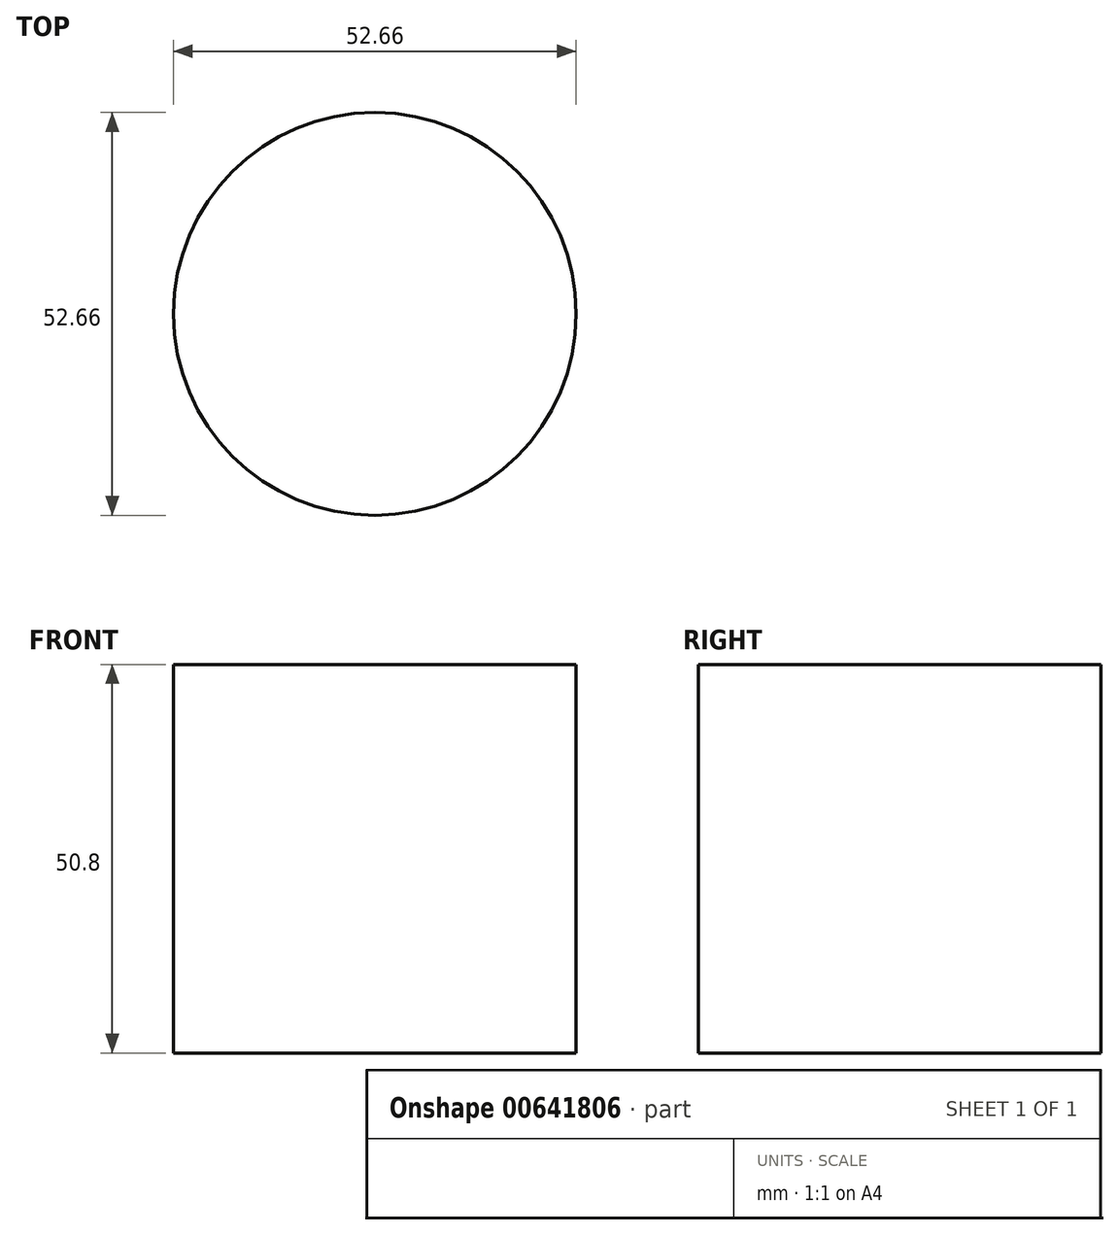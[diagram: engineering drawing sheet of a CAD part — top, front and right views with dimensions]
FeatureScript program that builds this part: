
annotation { "Feature Type Name" : "Feature", "Feature Type Description" : "" }
export const myFeature = defineFeature(function(context is Context, id is Id, definition is map)
    precondition{}
    {
        {
            var Q0;
            Q0=qCreatedBy(makeId("Top.planeOp"),FACE);
            var sketch = newSketch(context, id + "F0", { "sketchPlane" : qUnion([Q0])});
            skCircle(sketch, "E0", {"center": v(-45.91, 43.3) * mm, "radius": 26.33 * mm});
            skLineSegment(sketch, "E1", {"start": v(-63.2, 63.17) * mm, "end": v(-28.63, 23.45) * mm});
            skLineSegment(sketch, "E2", {"start": v(-38.25, 34.5) * mm, "end": v(-56.05, 19.01) * mm});
            skLineSegment(sketch, "E3", {"start": v(-54.32, 52.97) * mm, "end": v(-71.67, 37.87) * mm});
            skLineSegment(sketch, "E4", {"start": v(-28.63, 23.45) * mm, "end": v(-38.25, 34.5) * mm});
            skLineSegment(sketch, "E5", {"start": v(-63.2, 63.17) * mm, "end": v(-52.87, 51.3) * mm});
            skLineSegment(sketch, "E6", {"start": v(-52.87, 51.3) * mm, "end": v(-63.2, 63.17) * mm});
            skSolve(sketch);
        }
        {
            var Q0;
            {var subQ1=sQuery(id+"F0.wireOp",EDGE,"E1");Q0=makeQuery(id+"F0.imprint","IMPRINT",FACE,{"disambiguationData":[TD([[makeQuery(id+"F0.imprint","IMPRINT",EDGE,{"derivedFrom":subQ1}),1.0]])]});}
            var Q1;
            {var subQ1=sQuery(id+"F0.wireOp",EDGE,"E1");Q1=makeQuery(id+"F0.imprint","IMPRINT",FACE,{"disambiguationData":[TD([[makeQuery(id+"F0.imprint","IMPRINT",EDGE,{"derivedFrom":subQ1}),-1.0]])]});}
            var Q2;
            {var subQ0=sQuery(id+"F0.wireOp",EDGE,"E3");Q2=makeQuery(id+"F0.imprint","IMPRINT",FACE,{"disambiguationData":[TD([[makeQuery(id+"F0.imprint","IMPRINT",EDGE,{"derivedFrom":subQ0}),-1.0]])]});}
            var Q3;
            {var subQ0=sQuery(id+"F0.wireOp",EDGE,"E2");Q3=makeQuery(id+"F0.imprint","IMPRINT",FACE,{"disambiguationData":[TD([[makeQuery(id+"F0.imprint","IMPRINT",EDGE,{"derivedFrom":subQ0}),1.0]])]});}
            extrude(context, id + "F1", {"entities" : qUnion([Q0, Q1, Q2, Q3]), "depth" : 50.8 * mm, "offsetDistance" : 25.4 * mm});
        }
    });
